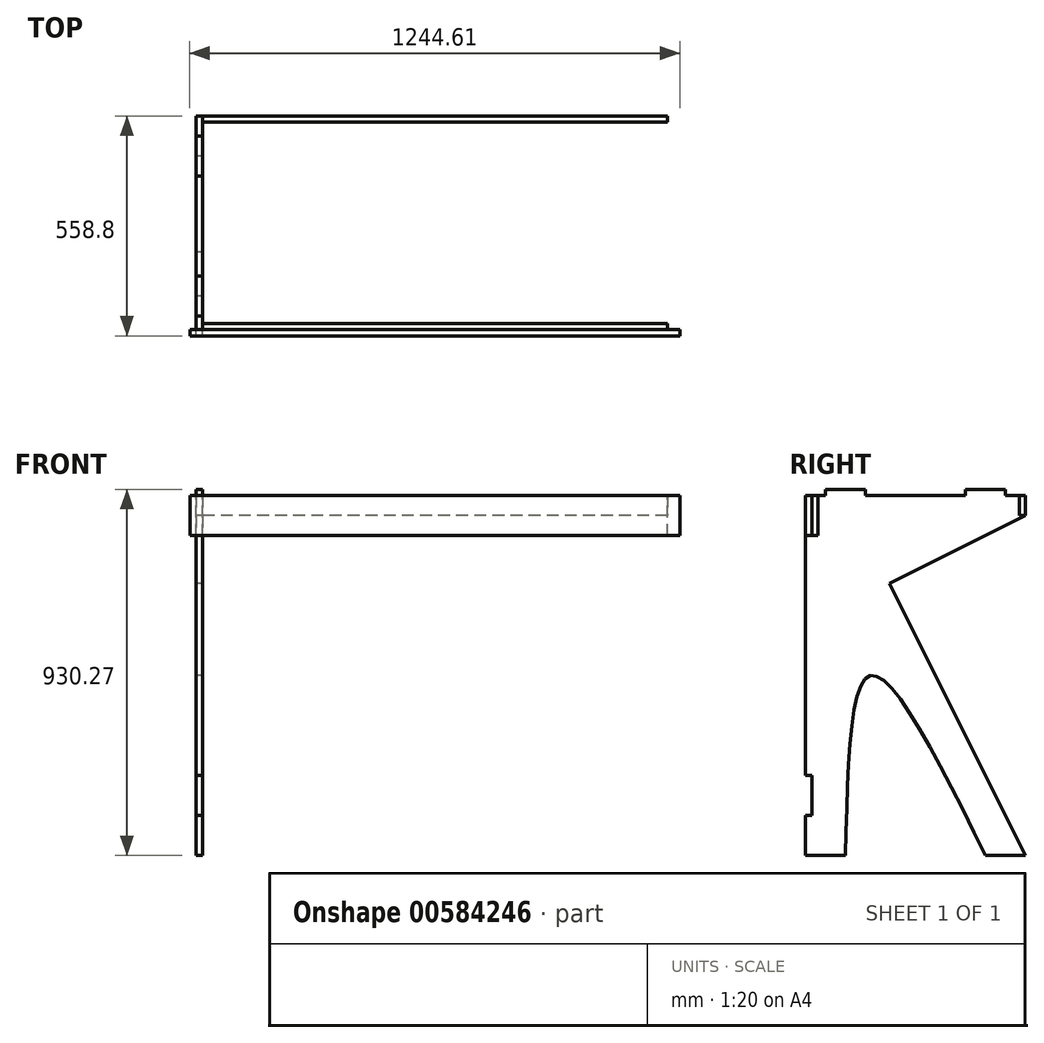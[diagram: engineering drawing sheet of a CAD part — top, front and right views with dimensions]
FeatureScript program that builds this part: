
annotation { "Feature Type Name" : "Feature", "Feature Type Description" : "" }
export const myFeature = defineFeature(function(context is Context, id is Id, definition is map)
    precondition{}
    {
        {
            var Q0;
            Q0=qCreatedBy(makeId("Right.planeOp"),FACE);
            var sketch = newSketch(context, id + "F0", { "sketchPlane" : qUnion([Q0])});
            skLineSegment(sketch, "E0", {"start": v(-508, 489.68) * mm, "end": v(-508, -119.92) * mm});
            skLineSegment(sketch, "E1", {"start": v(-508, -323.12) * mm, "end": v(-406.4, -323.12) * mm});
            skLineSegment(sketch, "E2", {"start": v(-492.13, 591.28) * mm, "end": v(-457.2, 591.28) * mm});
            skLineSegment(sketch, "E3", {"start": v(50.8, 591.28) * mm, "end": v(50.8, 540.48) * mm});
            skLineSegment(sketch, "E4", {"start": v(0, 591.28) * mm, "end": v(0, 607.15) * mm});
            skLineSegment(sketch, "E5", {"start": v(0, 607.15) * mm, "end": v(-101.6, 607.15) * mm});
            skLineSegment(sketch, "E6", {"start": v(-101.6, 607.15) * mm, "end": v(-101.6, 591.28) * mm});
            skLineSegment(sketch, "E7", {"start": v(-457.2, 591.28) * mm, "end": v(-457.2, 607.15) * mm});
            skLineSegment(sketch, "E8", {"start": v(-457.2, 607.15) * mm, "end": v(-355.6, 607.15) * mm});
            skLineSegment(sketch, "E9", {"start": v(-355.6, 607.15) * mm, "end": v(-355.6, 591.28) * mm});
            skLineSegment(sketch, "E10.trimOffspring", {"start": v(-355.6, 591.28) * mm, "end": v(-101.6, 591.28) * mm});
            skLineSegment(sketch, "E11.trimOffspring", {"start": v(0, 591.28) * mm, "end": v(50.8, 591.28) * mm});
            skPoint(sketch, "E12", {"position": v(-406.4, 591.28) * mm});
            skPoint(sketch, "E12.positionSnap0", {"position": v(-406.4, 607.15) * mm});
            skLineSegment(sketch, "E13", {"start": v(-294.64, 367.76) * mm, "end": v(50.8, -323.12) * mm});
            skLineSegment(sketch, "E14", {"start": v(50.8, -323.12) * mm, "end": v(-50.8, -323.12) * mm});
            skLineSegment(sketch, "E15", {"start": v(50.8, 540.48) * mm, "end": v(-294.64, 367.76) * mm});
            skLineSegment(sketch, "E16", {"start": v(-508, 134.08) * mm, "end": v(-177.8, 134.08) * mm, "construction": true});
            skFitSpline(sketch, "E17", {"points": [v(-406.4, -323.12) * mm, v(-342.9, 134.08) * mm, v(-50.8, -323.12) * mm], "startDerivative": vector(29.38, 1392.33) * mm, "endDerivative": vector(673.16, -1355.35) * mm});
            skPoint(sketch, "E18", {"position": v(-508, 489.68) * mm});
            skPoint(sketch, "E19", {"position": v(-508, -221.52) * mm});
            skLineSegment(sketch, "E20", {"start": v(-508, 489.68) * mm, "end": v(-492.13, 489.68) * mm});
            skLineSegment(sketch, "E21", {"start": v(-492.13, 489.68) * mm, "end": v(-492.13, 591.28) * mm});
            skPoint(sketch, "E22.orphan", {"position": v(-508, 591.28) * mm});
            skLineSegment(sketch, "E23.bottom", {"start": v(-508, -221.52) * mm, "end": v(-492.13, -221.52) * mm});
            skLineSegment(sketch, "E23.top", {"start": v(-508, -119.92) * mm, "end": v(-492.13, -119.92) * mm});
            skLineSegment(sketch, "E23.right", {"start": v(-492.13, -221.52) * mm, "end": v(-492.13, -119.92) * mm});
            skLineSegment(sketch, "E24.trimOffspring", {"start": v(-508, -221.52) * mm, "end": v(-508, -323.12) * mm});
            skSolve(sketch);
        }
        {
            var Q0;
            Q0=makeQuery(id+"F0.imprint","IMPRINT",FACE,{"disambiguationData":[TD([[makeQuery(id+"F0.imprint","IMPRINT",EDGE,{"derivedFrom":sQuery(id+"F0.wireOp",EDGE,"E0")}),1.0]])]});
            extrude(context, id + "F1", {"entities" : qUnion([Q0]), "depth" : 15.88 * mm, "offsetDistance" : 25.4 * mm});
        }
        {
            var Q0;
            Q0=makeQuery(id+"F1.opExtrude","CAP_FACE",FACE,{"disambiguationData":[OSD([sQuery(id+"F0.wireOp",EDGE,"E0"),sQuery(id+"F0.wireOp",EDGE,"E1"),sQuery(id+"F0.wireOp",EDGE,"E2"),sQuery(id+"F0.wireOp",EDGE,"E3"),sQuery(id+"F0.wireOp",EDGE,"E4"),sQuery(id+"F0.wireOp",EDGE,"E5"),sQuery(id+"F0.wireOp",EDGE,"E6"),sQuery(id+"F0.wireOp",EDGE,"E7"),sQuery(id+"F0.wireOp",EDGE,"E8"),sQuery(id+"F0.wireOp",EDGE,"E9"),sQuery(id+"F0.wireOp",EDGE,"E10.trimOffspring"),sQuery(id+"F0.wireOp",EDGE,"E11.trimOffspring"),sQuery(id+"F0.wireOp",EDGE,"E13"),sQuery(id+"F0.wireOp",EDGE,"E14"),sQuery(id+"F0.wireOp",EDGE,"E15"),sQuery(id+"F0.wireOp",EDGE,"E17"),sQuery(id+"F0.wireOp",EDGE,"E20"),sQuery(id+"F0.wireOp",EDGE,"E21"),sQuery(id+"F0.wireOp",EDGE,"E23.bottom"),sQuery(id+"F0.wireOp",EDGE,"E23.top"),sQuery(id+"F0.wireOp",EDGE,"E23.right"),sQuery(id+"F0.wireOp",EDGE,"E24.trimOffspring")])],"isStart":false});
            var sketch = newSketch(context, id + "F2", { "sketchPlane" : qUnion([Q0])});
            skLineSegment(sketch, "E25.bottom", {"start": v(50.8, 591.28) * mm, "end": v(34.93, 591.28) * mm});
            skLineSegment(sketch, "E25.top", {"start": v(50.8, 540.48) * mm, "end": v(34.93, 540.48) * mm});
            skLineSegment(sketch, "E25.left", {"start": v(50.8, 591.28) * mm, "end": v(50.8, 540.48) * mm});
            skLineSegment(sketch, "E25.right", {"start": v(34.93, 591.28) * mm, "end": v(34.93, 540.48) * mm});
            skSolve(sketch);
        }
        {
            var Q0;
            Q0=makeQuery(id+"F2.imprint","IMPRINT",FACE,{"disambiguationData":[TD([[makeQuery(id+"F2.imprint","IMPRINT",EDGE,{"derivedFrom":sQuery(id+"F2.wireOp",EDGE,"E25.bottom")}),-1.0]])]});
            extrude(context, id + "F3", {"entities" : qUnion([Q0]), "depth" : 1181.1 * mm, "offsetDistance" : 25.4 * mm});
        }
        {
            var Q0;
            Q0=makeQuery(id+"F1.opExtrude","CAP_FACE",FACE,{"disambiguationData":[OSD([sQuery(id+"F0.wireOp",EDGE,"E0"),sQuery(id+"F0.wireOp",EDGE,"E1"),sQuery(id+"F0.wireOp",EDGE,"E2"),sQuery(id+"F0.wireOp",EDGE,"E3"),sQuery(id+"F0.wireOp",EDGE,"E4"),sQuery(id+"F0.wireOp",EDGE,"E5"),sQuery(id+"F0.wireOp",EDGE,"E6"),sQuery(id+"F0.wireOp",EDGE,"E7"),sQuery(id+"F0.wireOp",EDGE,"E8"),sQuery(id+"F0.wireOp",EDGE,"E9"),sQuery(id+"F0.wireOp",EDGE,"E10.trimOffspring"),sQuery(id+"F0.wireOp",EDGE,"E11.trimOffspring"),sQuery(id+"F0.wireOp",EDGE,"E13"),sQuery(id+"F0.wireOp",EDGE,"E14"),sQuery(id+"F0.wireOp",EDGE,"E15"),sQuery(id+"F0.wireOp",EDGE,"E17"),sQuery(id+"F0.wireOp",EDGE,"E20"),sQuery(id+"F0.wireOp",EDGE,"E21"),sQuery(id+"F0.wireOp",EDGE,"E23.bottom"),sQuery(id+"F0.wireOp",EDGE,"E23.top"),sQuery(id+"F0.wireOp",EDGE,"E23.right"),sQuery(id+"F0.wireOp",EDGE,"E24.trimOffspring")])],"isStart":false});
            var sketch = newSketch(context, id + "F4", { "sketchPlane" : qUnion([Q0])});
            skLineSegment(sketch, "E26.bottom", {"start": v(-492.13, 591.28) * mm, "end": v(-476.25, 591.28) * mm});
            skLineSegment(sketch, "E26.top", {"start": v(-492.13, 489.68) * mm, "end": v(-476.25, 489.68) * mm});
            skLineSegment(sketch, "E26.left", {"start": v(-492.13, 591.28) * mm, "end": v(-492.13, 489.68) * mm});
            skLineSegment(sketch, "E26.right", {"start": v(-476.25, 591.28) * mm, "end": v(-476.25, 489.68) * mm});
            skSolve(sketch);
        }
        {
            var Q0;
            Q0=makeQuery(id+"F4.imprint","IMPRINT",FACE,{"disambiguationData":[TD([[makeQuery(id+"F4.imprint","IMPRINT",EDGE,{"derivedFrom":sQuery(id+"F4.wireOp",EDGE,"E26.bottom")}),-1.0]])]});
            extrude(context, id + "F5", {"entities" : qUnion([Q0]), "depth" : 1181.1 * mm, "offsetDistance" : 25.4 * mm});
        }
        {
            var Q0;
            Q0=makeQuery(id+"F1.opExtrude","CAP_FACE",FACE,{"disambiguationData":[OSD([sQuery(id+"F0.wireOp",EDGE,"E0"),sQuery(id+"F0.wireOp",EDGE,"E1"),sQuery(id+"F0.wireOp",EDGE,"E2"),sQuery(id+"F0.wireOp",EDGE,"E3"),sQuery(id+"F0.wireOp",EDGE,"E4"),sQuery(id+"F0.wireOp",EDGE,"E5"),sQuery(id+"F0.wireOp",EDGE,"E6"),sQuery(id+"F0.wireOp",EDGE,"E7"),sQuery(id+"F0.wireOp",EDGE,"E8"),sQuery(id+"F0.wireOp",EDGE,"E9"),sQuery(id+"F0.wireOp",EDGE,"E10.trimOffspring"),sQuery(id+"F0.wireOp",EDGE,"E11.trimOffspring"),sQuery(id+"F0.wireOp",EDGE,"E13"),sQuery(id+"F0.wireOp",EDGE,"E14"),sQuery(id+"F0.wireOp",EDGE,"E15"),sQuery(id+"F0.wireOp",EDGE,"E17"),sQuery(id+"F0.wireOp",EDGE,"E20"),sQuery(id+"F0.wireOp",EDGE,"E21"),sQuery(id+"F0.wireOp",EDGE,"E23.bottom"),sQuery(id+"F0.wireOp",EDGE,"E23.top"),sQuery(id+"F0.wireOp",EDGE,"E23.right"),sQuery(id+"F0.wireOp",EDGE,"E24.trimOffspring")])],"isStart":false});
            var sketch = newSketch(context, id + "F6", { "sketchPlane" : qUnion([Q0])});
            skLineSegment(sketch, "E27.bottom", {"start": v(-492.13, 489.68) * mm, "end": v(-508, 489.68) * mm});
            skLineSegment(sketch, "E27.top", {"start": v(-492.13, 591.28) * mm, "end": v(-508, 591.28) * mm});
            skLineSegment(sketch, "E27.left", {"start": v(-492.13, 489.68) * mm, "end": v(-492.13, 591.28) * mm});
            skLineSegment(sketch, "E27.right", {"start": v(-508, 489.68) * mm, "end": v(-508, 591.28) * mm});
            skSolve(sketch);
        }
        {
            var Q0;
            Q0=makeQuery(id+"F6.imprint","IMPRINT",FACE,{"disambiguationData":[TD([[makeQuery(id+"F6.imprint","IMPRINT",EDGE,{"derivedFrom":sQuery(id+"F6.wireOp",EDGE,"E27.bottom")}),1.0]])]});
            extrude(context, id + "F7", {"entities" : qUnion([Q0]), "depth" : 1212.85 * mm, "offsetDistance" : 25.4 * mm, "hasSecondDirection" : true, "secondDirectionOppositeDirection" : true, "secondDirectionDepth" : 31.75 * mm});
        }
    });
